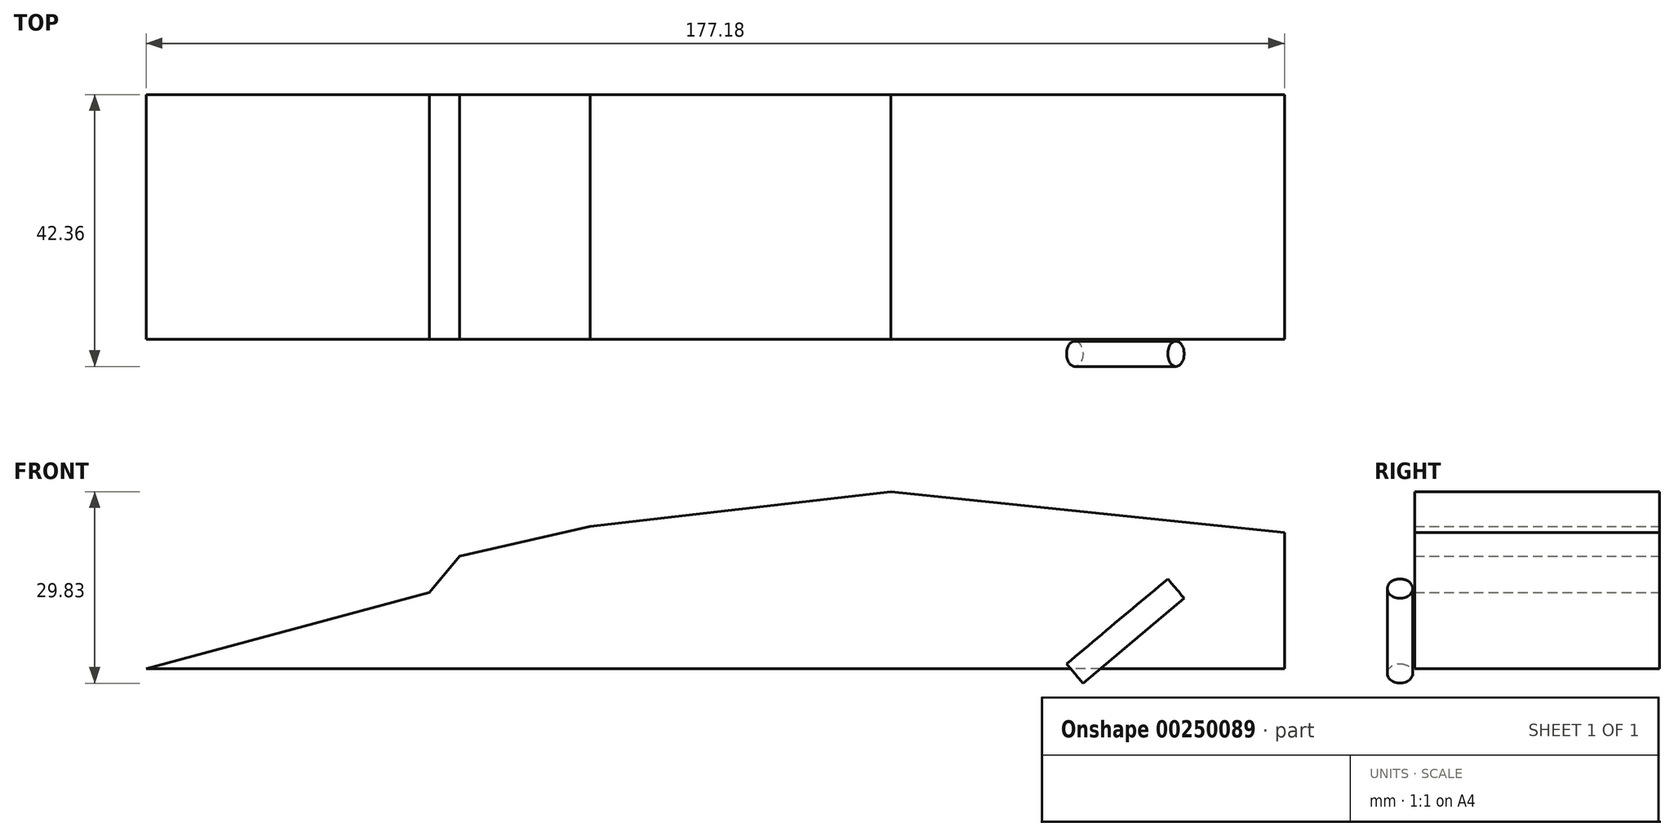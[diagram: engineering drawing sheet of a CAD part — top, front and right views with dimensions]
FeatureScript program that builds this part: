
annotation { "Feature Type Name" : "Feature", "Feature Type Description" : "" }
export const myFeature = defineFeature(function(context is Context, id is Id, definition is map)
    precondition{}
    {
        {
            var Q0;
            Q0=qCreatedBy(makeId("Front.planeOp"),FACE);
            var sketch = newSketch(context, id + "F0", { "sketchPlane" : qUnion([Q0])});
            skLineSegment(sketch, "E0", {"start": v(-100.23, 0) * mm, "end": v(-56.12, 11.89) * mm});
            skLineSegment(sketch, "E1", {"start": v(-56.12, 11.89) * mm, "end": v(-51.46, 17.52) * mm});
            skLineSegment(sketch, "E2", {"start": v(-51.46, 17.52) * mm, "end": v(-31.12, 22.18) * mm});
            skLineSegment(sketch, "E3", {"start": v(-31.12, 22.18) * mm, "end": v(15.68, 27.57) * mm});
            skLineSegment(sketch, "E4", {"start": v(15.68, 27.57) * mm, "end": v(76.95, 21.2) * mm});
            skLineSegment(sketch, "E5", {"start": v(76.95, 21.2) * mm, "end": v(76.95, 0) * mm});
            skLineSegment(sketch, "E6", {"start": v(76.95, 0) * mm, "end": v(-100.23, 0) * mm});
            skSolve(sketch);
        }
        {
            var Q0;
            Q0=makeQuery(id+"F0.imprint","IMPRINT",FACE,{"disambiguationData":[TD([[makeQuery(id+"F0.imprint","IMPRINT",EDGE,{"derivedFrom":sQuery(id+"F0.wireOp",EDGE,"E0")}),-1.0]])]});
            extrude(context, id + "F1", {"entities" : qUnion([Q0]), "depth" : 38.1 * mm});
        }
        {
            var Q0;
            Q0=makeQuery(id+"F1.opExtrude","SWEPT_EDGE",EDGE,{"disambiguationData":[OSD([sQuery(id+"F0.wireOp",EDGE,"E4"),sQuery(id+"F0.wireOp",EDGE,"E5")])]});
            var Q1;
            Q1=qCreatedBy(makeId("Right.planeOp"),FACE);
            cPlane(context, id + "F2", {"entities" : qUnion([Q0, Q1]), "cplaneType" : CPlaneType.LINE_ANGLE, "offset" : 25.4 * mm, "angle" : 40 * degree, "oppositeDirection" : true, "width" : 152.4 * mm, "height" : 152.4 * mm});
        }
        {
            var Q0;
            Q0=qCreatedBy(id+"F2.planeOp",FACE);
            var sketch = newSketch(context, id + "F3", { "sketchPlane" : qUnion([Q0])});
            skCircle(sketch, "E7", {"center": v(40.39, -29.05) * mm, "radius": 1.97 * mm});
            skCircle(sketch, "E8", {"center": v(40.9, -23.83) * mm, "radius": 2.14 * mm});
            skCircle(sketch, "E9", {"center": v(41.17, -20.64) * mm, "radius": 2.25 * mm});
            skCircle(sketch, "E10", {"center": v(41.48, -15.5) * mm, "radius": 2.12 * mm});
            skSolve(sketch);
        }
        {
            var Q0;
            Q0=makeQuery(id+"F3.imprint","IMPRINT",FACE,{"disambiguationData":[TD([[makeQuery(id+"F3.imprint","IMPRINT",EDGE,{"derivedFrom":sQuery(id+"F3.wireOp",EDGE,"E7")}),1.0]])]});
            var Q1;
            Q1=sQuery(id+"F3.wireOp",EDGE,"E7");
            extrude(context, id + "F4", {"entities" : qUnion([Q0]), "surfaceEntities" : qUnion([Q1]), "depth" : 39.12 * mm, "hasSecondDirection" : true, "secondDirectionOppositeDirection" : false, "secondDirectionDepth" : 18.54 * mm});
        }
    });
